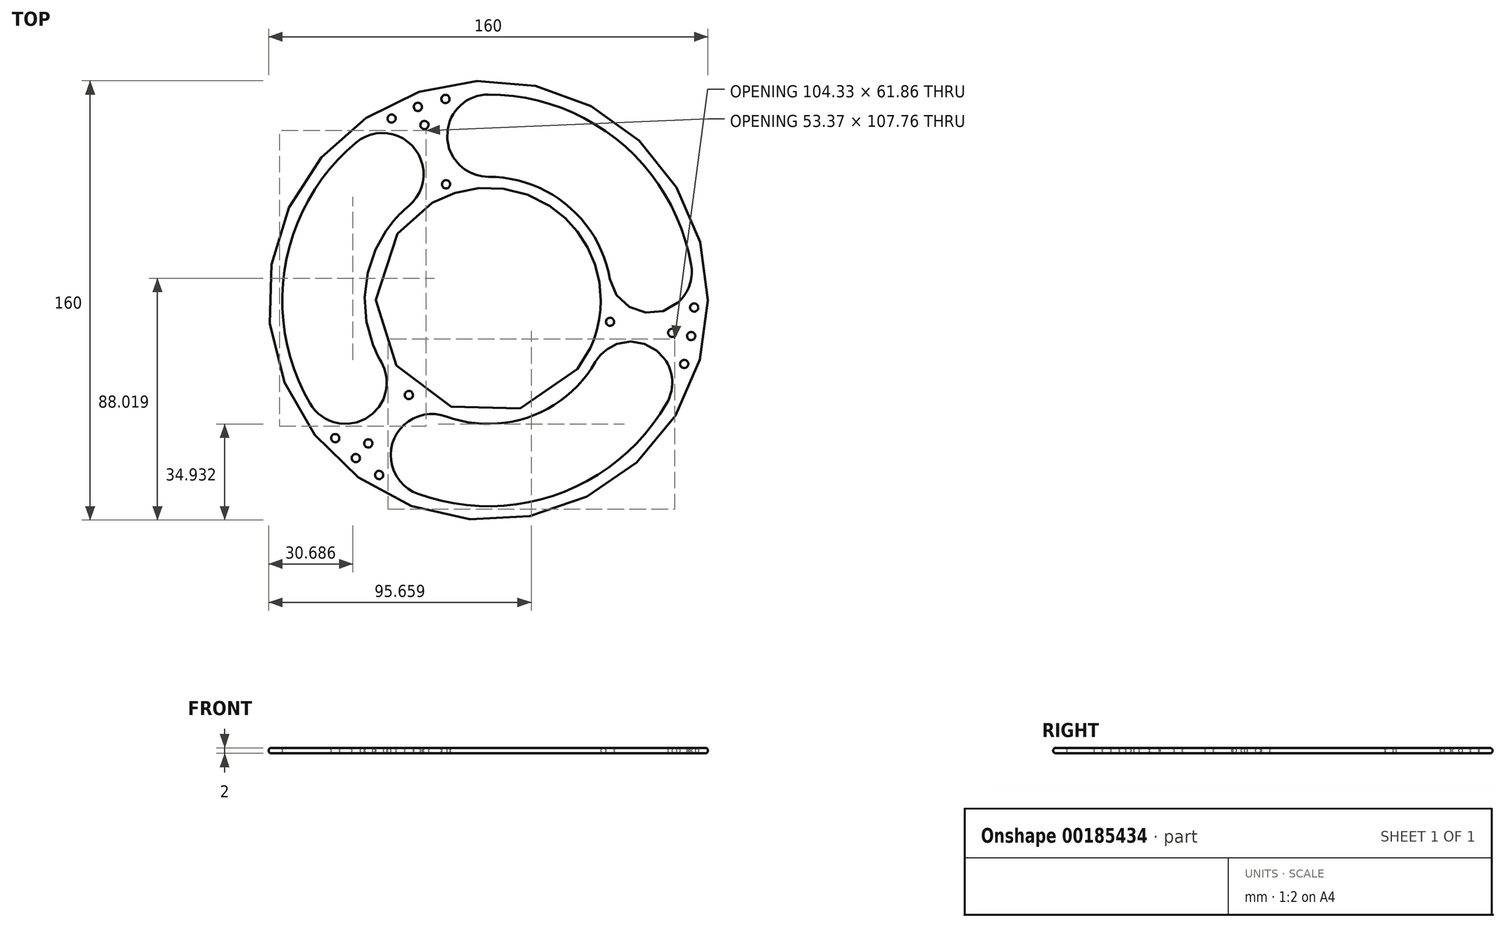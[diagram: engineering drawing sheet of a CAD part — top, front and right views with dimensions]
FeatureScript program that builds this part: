
annotation { "Feature Type Name" : "Feature", "Feature Type Description" : "" }
export const myFeature = defineFeature(function(context is Context, id is Id, definition is map)
    precondition{}
    {
        {
            var Q0;
            Q0=qCreatedBy(makeId("Top.planeOp"),FACE);
            var sketch = newSketch(context, id + "F0", { "sketchPlane" : qUnion([Q0])});
            skCircle(sketch, "E0", {"center": v(0, 0) * mm, "radius": 41 * mm});
            skCircle(sketch, "E1", {"center": v(0, 0) * mm, "radius": 80 * mm});
            skPoint(sketch, "E2", {"position": v(0, 41) * mm});
            skCircle(sketch, "E3", {"center": v(0, 60) * mm, "radius": 15 * mm});
            skCircle(sketch, "E4.1.0", {"center": v(-38.57, 45.96) * mm, "radius": 15 * mm});
            skCircle(sketch, "E4.2.0", {"center": v(-59.09, 10.42) * mm, "radius": 15 * mm});
            skCircle(sketch, "E4.3.0", {"center": v(-51.96, -30) * mm, "radius": 15 * mm});
            skCircle(sketch, "E4.4.0", {"center": v(-20.52, -56.38) * mm, "radius": 15 * mm});
            skCircle(sketch, "E4.5.0", {"center": v(20.52, -56.38) * mm, "radius": 15 * mm});
            skCircle(sketch, "E4.6.0", {"center": v(51.96, -30) * mm, "radius": 15 * mm});
            skCircle(sketch, "E4.7.0", {"center": v(59.09, 10.42) * mm, "radius": 15 * mm});
            skCircle(sketch, "E4.8.0", {"center": v(38.57, 45.96) * mm, "radius": 15 * mm});
            skCircle(sketch, "E5", {"center": v(0, 0) * mm, "radius": 45 * mm});
            skCircle(sketch, "E6", {"center": v(0, 0) * mm, "radius": 75 * mm});
            skLineSegment(sketch, "E7", {"start": v(0, 0) * mm, "end": v(0, 80) * mm, "construction": true});
            skLineSegment(sketch, "E8", {"start": v(0, 0) * mm, "end": v(-16.63, 78.25) * mm, "construction": true});
            skLineSegment(sketch, "E9", {"start": v(0, 0) * mm, "end": v(-27.36, 75.18) * mm, "construction": true});
            skLineSegment(sketch, "E10", {"start": v(0, 0) * mm, "end": v(-37.56, 70.64) * mm, "construction": true});
            skCircle(sketch, "E11", {"center": v(-35.21, 66.22) * mm, "radius": 1.5 * mm});
            skCircle(sketch, "E12", {"center": v(-25.65, 70.48) * mm, "radius": 1.5 * mm});
            skCircle(sketch, "E13", {"center": v(-15.6, 73.36) * mm, "radius": 1.5 * mm});
            skCircle(sketch, "E14", {"center": v(-23.26, 63.9) * mm, "radius": 1.5 * mm});
            skCircle(sketch, "E15", {"center": v(-15.4, 42.29) * mm, "radius": 1.5 * mm});
            skCircle(sketch, "E16.1.0", {"center": v(-39.74, -63.6) * mm, "radius": 1.5 * mm});
            skCircle(sketch, "E16.1.1", {"center": v(-48.2, -57.45) * mm, "radius": 1.5 * mm});
            skCircle(sketch, "E16.1.2", {"center": v(-55.74, -50.18) * mm, "radius": 1.5 * mm});
            skCircle(sketch, "E16.1.3", {"center": v(-43.7, -52.1) * mm, "radius": 1.5 * mm});
            skCircle(sketch, "E16.1.4", {"center": v(-28.93, -34.47) * mm, "radius": 1.5 * mm});
            skCircle(sketch, "E16.2.0", {"center": v(74.95, -2.62) * mm, "radius": 1.5 * mm});
            skCircle(sketch, "E16.2.1", {"center": v(73.86, -13.02) * mm, "radius": 1.5 * mm});
            skCircle(sketch, "E16.2.2", {"center": v(71.33, -23.18) * mm, "radius": 1.5 * mm});
            skCircle(sketch, "E16.2.3", {"center": v(66.97, -11.8) * mm, "radius": 1.5 * mm});
            skCircle(sketch, "E16.2.4", {"center": v(44.32, -7.81) * mm, "radius": 1.5 * mm});
            skSolve(sketch);
        }
        {
            var Q0;
            Q0=makeQuery(id+"F0.imprint","IMPRINT",FACE,{"disambiguationData":[TD([[makeQuery(id+"F0.imprint","IMPRINT",EDGE,{"derivedFrom":sQuery(id+"F0.wireOp",EDGE,"E0")}),-1.0]])]});
            var Q1;
            Q1=makeQuery(id+"F0.imprint","IMPRINT",FACE,{"disambiguationData":[TD([[makeQuery(id+"F0.imprint","IMPRINT",EDGE,{"derivedFrom":sQuery(id+"F0.wireOp",EDGE,"E1")}),1.0]])]});
            var Q2;
            Q2=makeQuery(id+"F0.imprint","IMPRINT",FACE,{"disambiguationData":[TD([[makeQuery(id+"F0.imprint","IMPRINT",EDGE,{"derivedFrom":sQuery(id+"F0.wireOp",EDGE,"12144231-284d-4df9-a641-a248ca5025e5")}),1.0]])]});
            var Q3;
            Q3=makeQuery(id+"F0.imprint","IMPRINT",FACE,{"disambiguationData":[TD([[makeQuery(id+"F0.imprint","IMPRINT",EDGE,{"derivedFrom":sQuery(id+"F0.wireOp",EDGE,"39315ff6-fe9a-4697-a772-5aedfbdf977a")}),-1.0]])]});
            var Q4;
            {var subQ0=sQuery(id+"F0.wireOp",EDGE,"E5");var subQ6=sQuery(id+"F0.wireOp",EDGE,"E4.1.0");var subQ8=makeQuery(id+"F0.imprint","INTERSECT",VERTEX,{"derivedFrom":[subQ6,subQ0]});Q4=makeQuery(id+"F0.imprint","IMPRINT",FACE,{"disambiguationData":[TD([[makeQuery(id+"F0.imprint","IMPRINT",EDGE,{"disambiguationData":[TD([[subQ8,-1.0]])],"derivedFrom":subQ6}),-1.0]])]});}
            var Q5;
            {var subQ0=sQuery(id+"F0.wireOp",EDGE,"E5");var subQ1=sQuery(id+"F0.wireOp",EDGE,"E4.3.0");var subQ2=makeQuery(id+"F0.imprint","INTERSECT",VERTEX,{"derivedFrom":[subQ1,subQ0]});Q5=makeQuery(id+"F0.imprint","IMPRINT",FACE,{"disambiguationData":[TD([[makeQuery(id+"F0.imprint","IMPRINT",EDGE,{"disambiguationData":[TD([[subQ2,1.0]])],"derivedFrom":subQ1}),-1.0]])]});}
            var Q6;
            {var subQ0=sQuery(id+"F0.wireOp",EDGE,"E5");var subQ1=sQuery(id+"F0.wireOp",EDGE,"E4.6.0");var subQ2=makeQuery(id+"F0.imprint","INTERSECT",VERTEX,{"derivedFrom":[subQ1,subQ0]});Q6=makeQuery(id+"F0.imprint","IMPRINT",FACE,{"disambiguationData":[TD([[makeQuery(id+"F0.imprint","IMPRINT",EDGE,{"disambiguationData":[TD([[subQ2,1.0]])],"derivedFrom":subQ1}),-1.0]])]});}
            var Q7;
            {var subQ0=sQuery(id+"F0.wireOp",EDGE,"iCRS4vvn-fK7k-q4lI-TTiO-BZisHl7NfkP5");var subQ1=sQuery(id+"F0.wireOp",EDGE,"d2278acb-94d0-4041-99c4-45640f80405a.2.0");var subQ2=makeQuery(id+"F0.imprint","INTERSECT",VERTEX,{"derivedFrom":[subQ1,subQ0]});Q7=makeQuery(id+"F0.imprint","IMPRINT",FACE,{"disambiguationData":[TD([[makeQuery(id+"F0.imprint","IMPRINT",EDGE,{"disambiguationData":[TD([[subQ2,1.0]])],"derivedFrom":subQ1}),-1.0]])]});}
            var Q8;
            {var subQ0=sQuery(id+"F0.wireOp",EDGE,"iCRS4vvn-fK7k-q4lI-TTiO-BZisHl7NfkP5");var subQ6=sQuery(id+"F0.wireOp",EDGE,"d2278acb-94d0-4041-99c4-45640f80405a.8.0");var subQ7=makeQuery(id+"F0.imprint","INTERSECT",VERTEX,{"derivedFrom":[subQ6,subQ0]});Q8=makeQuery(id+"F0.imprint","IMPRINT",FACE,{"disambiguationData":[TD([[makeQuery(id+"F0.imprint","IMPRINT",EDGE,{"disambiguationData":[TD([[subQ7,1.0]])],"derivedFrom":subQ6}),-1.0]])]});}
            var Q9;
            {var subQ0=sQuery(id+"F0.wireOp",EDGE,"iCRS4vvn-fK7k-q4lI-TTiO-BZisHl7NfkP5");var subQ1=sQuery(id+"F0.wireOp",EDGE,"d2278acb-94d0-4041-99c4-45640f80405a.5.0");var subQ2=makeQuery(id+"F0.imprint","INTERSECT",VERTEX,{"derivedFrom":[subQ1,subQ0]});Q9=makeQuery(id+"F0.imprint","IMPRINT",FACE,{"disambiguationData":[TD([[makeQuery(id+"F0.imprint","IMPRINT",EDGE,{"disambiguationData":[TD([[subQ2,1.0]])],"derivedFrom":subQ1}),-1.0]])]});}
            extrude(context, id + "F1", {"entities" : qUnion([Q0, Q1, Q2, Q3, Q4, Q5, Q6, Q7, Q8, Q9]), "oppositeDirection" : true, "depth" : 2 * mm});
        }
        {
            var Q0;
            {var subQ0=sQuery(id+"F0.wireOp",EDGE,"E5");var subQ3=sQuery(id+"F0.wireOp",EDGE,"E4.3.0");var subQ4=sQuery(id+"F0.wireOp",EDGE,"E4.1.0");var subQ7=sQuery(id+"F0.wireOp",EDGE,"E3");var subQ9=sQuery(id+"F0.wireOp",EDGE,"E4.7.0");var subQ10=sQuery(id+"F0.wireOp",EDGE,"E4.6.0");var subQ11=sQuery(id+"F0.wireOp",EDGE,"E6");var subQ14=sQuery(id+"F0.wireOp",EDGE,"E4.4.0");var subQ15=sQuery(id+"F0.wireOp",EDGE,"91143b4f-f01d-424d-a080-ab716d14144e.1.0");var subQ16=sQuery(id+"F0.wireOp",EDGE,"DUbeLfhc-KFOZ-IpYY-nPxA-Tqe8eofQ2sMU");var subQ17=sQuery(id+"F0.wireOp",EDGE,"E1");var subQ18=sQuery(id+"F0.wireOp",EDGE,"ki0pbCab-z4uQ-DABq-K0KA-hCvC2e9yv8la");var subQ22=sQuery(id+"F0.wireOp",EDGE,"91143b4f-f01d-424d-a080-ab716d14144e.1.1");var subQ23=sQuery(id+"F0.wireOp",EDGE,"91143b4f-f01d-424d-a080-ab716d14144e.2.0");var subQ24=sQuery(id+"F0.wireOp",EDGE,"91143b4f-f01d-424d-a080-ab716d14144e.2.1");Q0=makeQuery(id+"F1.boolean.opBoolean","SPLIT",FACE,{"disambiguationData":[TD([makeQuery(id+"Fp+TmqwSZFw9QQVvP_0.opExtrude","SWEPT_FACE",FACE,{"disambiguationData":[OSD([sQuery(id+"F0.wireOp",EDGE,"E0")])]})])],"derivedFrom":makeQuery(id+"F1.opExtrude","CAP_FACE",FACE,{"disambiguationData":[OSD([sQuery(id+"F0.wireOp",EDGE,"39315ff6-fe9a-4697-a772-5aedfbdf977a"),subQ17,subQ7,sQuery(id+"F0.wireOp",EDGE,"088b27ed-a362-4ca8-a1c4-84918d803915"),subQ4,subQ3,subQ14,subQ10,subQ9,subQ0,subQ11,sQuery(id+"F0.wireOp",EDGE,"d2278acb-94d0-4041-99c4-45640f80405a.2.0"),sQuery(id+"F0.wireOp",EDGE,"d2278acb-94d0-4041-99c4-45640f80405a.3.0"),sQuery(id+"F0.wireOp",EDGE,"d2278acb-94d0-4041-99c4-45640f80405a.5.0"),sQuery(id+"F0.wireOp",EDGE,"d2278acb-94d0-4041-99c4-45640f80405a.6.0"),sQuery(id+"F0.wireOp",EDGE,"d2278acb-94d0-4041-99c4-45640f80405a.8.0"),sQuery(id+"F0.wireOp",EDGE,"iCRS4vvn-fK7k-q4lI-TTiO-BZisHl7NfkP5"),sQuery(id+"F0.wireOp",EDGE,"ewECKdEy-OtgB-HKcG-UGzn-Avy0xrEZuJEq"),subQ18,subQ16,subQ15,subQ22,subQ23,subQ24])],"isStart":true})});}
            var Q1;
            Q1=makeQuery(id+"F1.opExtrude","CAP_FACE",FACE,{"disambiguationData":[OSD([sQuery(id+"F0.wireOp",EDGE,"39315ff6-fe9a-4697-a772-5aedfbdf977a"),sQuery(id+"F0.wireOp",EDGE,"E1"),sQuery(id+"F0.wireOp",EDGE,"E3"),sQuery(id+"F0.wireOp",EDGE,"088b27ed-a362-4ca8-a1c4-84918d803915"),sQuery(id+"F0.wireOp",EDGE,"E4.1.0"),sQuery(id+"F0.wireOp",EDGE,"E4.3.0"),sQuery(id+"F0.wireOp",EDGE,"E4.4.0"),sQuery(id+"F0.wireOp",EDGE,"E4.6.0"),sQuery(id+"F0.wireOp",EDGE,"E4.7.0"),sQuery(id+"F0.wireOp",EDGE,"E5"),sQuery(id+"F0.wireOp",EDGE,"E6"),sQuery(id+"F0.wireOp",EDGE,"d2278acb-94d0-4041-99c4-45640f80405a.2.0"),sQuery(id+"F0.wireOp",EDGE,"d2278acb-94d0-4041-99c4-45640f80405a.3.0"),sQuery(id+"F0.wireOp",EDGE,"d2278acb-94d0-4041-99c4-45640f80405a.5.0"),sQuery(id+"F0.wireOp",EDGE,"d2278acb-94d0-4041-99c4-45640f80405a.6.0"),sQuery(id+"F0.wireOp",EDGE,"d2278acb-94d0-4041-99c4-45640f80405a.8.0"),sQuery(id+"F0.wireOp",EDGE,"iCRS4vvn-fK7k-q4lI-TTiO-BZisHl7NfkP5"),sQuery(id+"F0.wireOp",EDGE,"ewECKdEy-OtgB-HKcG-UGzn-Avy0xrEZuJEq"),sQuery(id+"F0.wireOp",EDGE,"ki0pbCab-z4uQ-DABq-K0KA-hCvC2e9yv8la"),sQuery(id+"F0.wireOp",EDGE,"DUbeLfhc-KFOZ-IpYY-nPxA-Tqe8eofQ2sMU"),sQuery(id+"F0.wireOp",EDGE,"91143b4f-f01d-424d-a080-ab716d14144e.1.0"),sQuery(id+"F0.wireOp",EDGE,"91143b4f-f01d-424d-a080-ab716d14144e.1.1"),sQuery(id+"F0.wireOp",EDGE,"91143b4f-f01d-424d-a080-ab716d14144e.2.0"),sQuery(id+"F0.wireOp",EDGE,"91143b4f-f01d-424d-a080-ab716d14144e.2.1")])],"isStart":false});
            var Q2;
            {var subQ0=sQuery(id+"F0.wireOp",EDGE,"iCRS4vvn-fK7k-q4lI-TTiO-BZisHl7NfkP5");var subQ3=sQuery(id+"F0.wireOp",EDGE,"d2278acb-94d0-4041-99c4-45640f80405a.2.0");var subQ4=sQuery(id+"F0.wireOp",EDGE,"088b27ed-a362-4ca8-a1c4-84918d803915");var subQ6=sQuery(id+"F0.wireOp",EDGE,"d2278acb-94d0-4041-99c4-45640f80405a.6.0");var subQ9=sQuery(id+"F0.wireOp",EDGE,"d2278acb-94d0-4041-99c4-45640f80405a.8.0");var subQ10=sQuery(id+"F0.wireOp",EDGE,"39315ff6-fe9a-4697-a772-5aedfbdf977a");var subQ11=sQuery(id+"F0.wireOp",EDGE,"d2278acb-94d0-4041-99c4-45640f80405a.5.0");var subQ12=sQuery(id+"F0.wireOp",EDGE,"d2278acb-94d0-4041-99c4-45640f80405a.3.0");var subQ13=sQuery(id+"F0.wireOp",EDGE,"ewECKdEy-OtgB-HKcG-UGzn-Avy0xrEZuJEq");Q2=makeQuery(id+"F1.boolean.opBoolean","SPLIT",FACE,{"disambiguationData":[TD([makeQuery(id+"Fp+TmqwSZFw9QQVvP_0.opExtrude","SWEPT_FACE",FACE,{"disambiguationData":[OSD([sQuery(id+"F0.wireOp",EDGE,"12144231-284d-4df9-a641-a248ca5025e5")])]})])],"derivedFrom":makeQuery(id+"F1.opExtrude","CAP_FACE",FACE,{"disambiguationData":[OSD([subQ10,sQuery(id+"F0.wireOp",EDGE,"E1"),sQuery(id+"F0.wireOp",EDGE,"E3"),subQ4,sQuery(id+"F0.wireOp",EDGE,"E4.1.0"),sQuery(id+"F0.wireOp",EDGE,"E4.3.0"),sQuery(id+"F0.wireOp",EDGE,"E4.4.0"),sQuery(id+"F0.wireOp",EDGE,"E4.6.0"),sQuery(id+"F0.wireOp",EDGE,"E4.7.0"),sQuery(id+"F0.wireOp",EDGE,"E5"),sQuery(id+"F0.wireOp",EDGE,"E6"),subQ3,subQ12,subQ11,subQ6,subQ9,subQ0,subQ13,sQuery(id+"F0.wireOp",EDGE,"ki0pbCab-z4uQ-DABq-K0KA-hCvC2e9yv8la"),sQuery(id+"F0.wireOp",EDGE,"DUbeLfhc-KFOZ-IpYY-nPxA-Tqe8eofQ2sMU"),sQuery(id+"F0.wireOp",EDGE,"91143b4f-f01d-424d-a080-ab716d14144e.1.0"),sQuery(id+"F0.wireOp",EDGE,"91143b4f-f01d-424d-a080-ab716d14144e.1.1"),sQuery(id+"F0.wireOp",EDGE,"91143b4f-f01d-424d-a080-ab716d14144e.2.0"),sQuery(id+"F0.wireOp",EDGE,"91143b4f-f01d-424d-a080-ab716d14144e.2.1")])],"isStart":true})});}
            fillet(context, id + "F2", {"entities" : qUnion([Q0, Q1, Q2]), "radius" : 1 * mm, "tangentPropagation" : true, "allowEdgeOverflow" : false});
        }
    });
